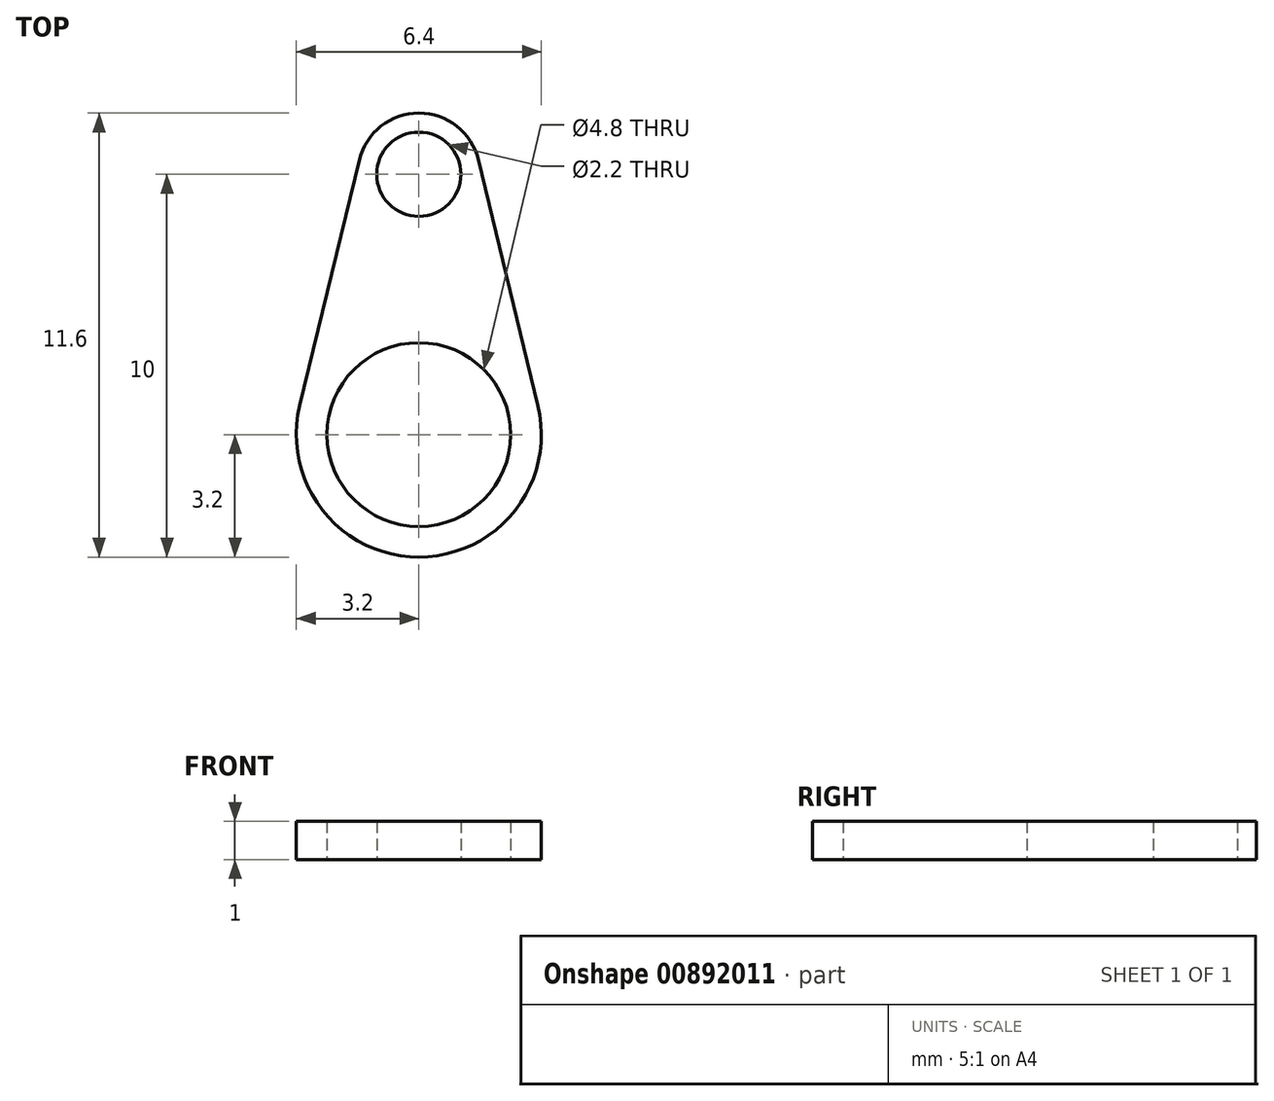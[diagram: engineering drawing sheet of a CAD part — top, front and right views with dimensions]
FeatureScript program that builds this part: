
annotation { "Feature Type Name" : "Feature", "Feature Type Description" : "" }
export const myFeature = defineFeature(function(context is Context, id is Id, definition is map)
    precondition{}
    {
        {
            var Q0;
            Q0=qCreatedBy(makeId("Top.planeOp"),FACE);
            var sketch = newSketch(context, id + "F0", { "sketchPlane" : qUnion([Q0])});
            skCircle(sketch, "E0", {"center": v(0, 0) * mm, "radius": 2.4 * mm});
            skCircle(sketch, "E1", {"center": v(0, 6.8) * mm, "radius": 1.1 * mm});
            skArc(sketch, "E2", {"start": v(1.56, 7.18) * mm, "mid": v(0, 8.4) * mm, "end": v(-1.56, 7.18) * mm});
            skArc(sketch, "E3", {"start": v(-3.11, 0.75) * mm, "mid": v(0, -3.2) * mm, "end": v(3.11, 0.75) * mm});
            skLineSegment(sketch, "E4", {"start": v(-1.56, 7.18) * mm, "end": v(-3.11, 0.75) * mm});
            skLineSegment(sketch, "E5.MirrorCS", {"start": v(1.56, 7.18) * mm, "end": v(3.11, 0.75) * mm});
            skSolve(sketch);
        }
        {
            var Q0;
            Q0=makeQuery(id+"F0.imprint","IMPRINT",FACE,{"disambiguationData":[TD([[makeQuery(id+"F0.imprint","IMPRINT",EDGE,{"derivedFrom":sQuery(id+"F0.wireOp",EDGE,"E0")}),-1.0]])]});
            extrude(context, id + "F1", {"entities" : qUnion([Q0]), "depth" : 1 * mm, "offsetDistance" : 25 * mm});
        }
    });
